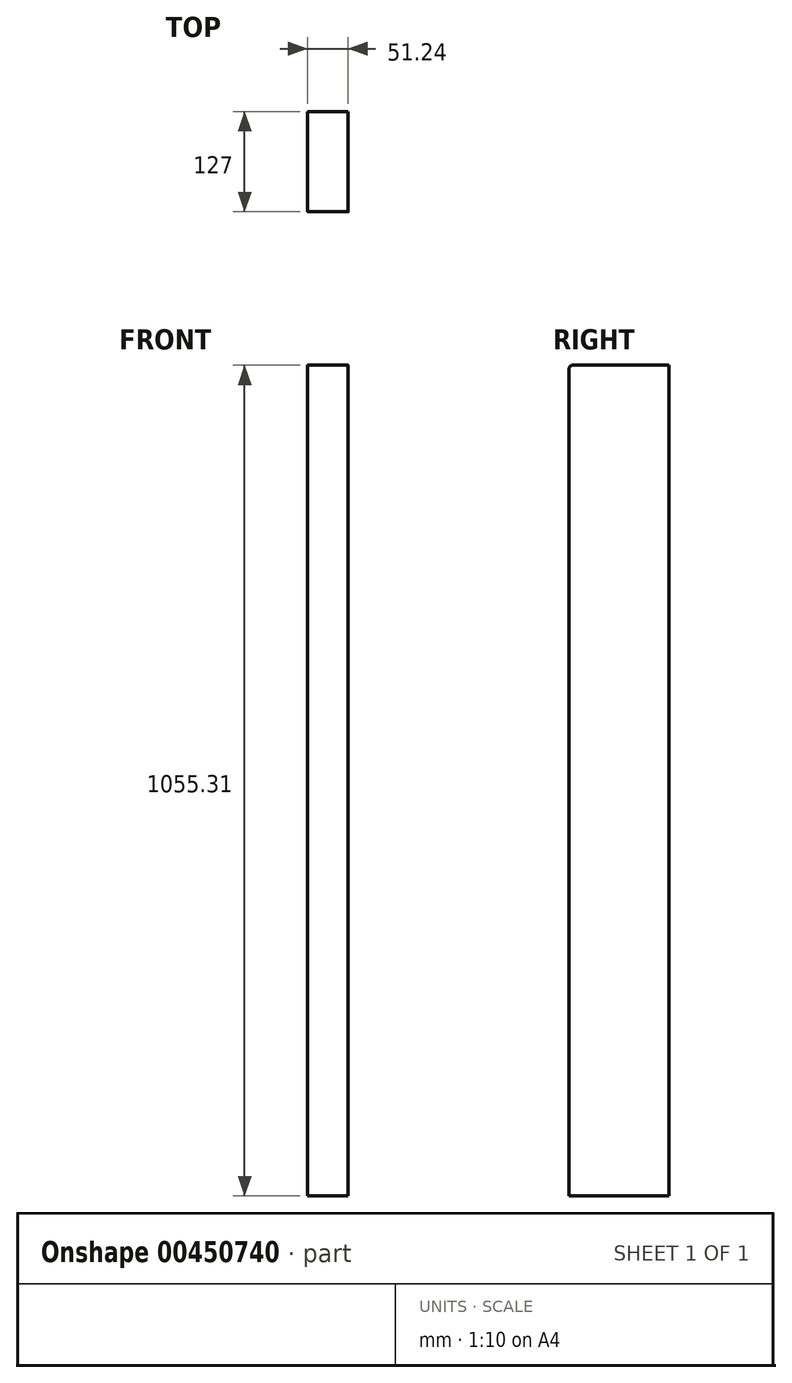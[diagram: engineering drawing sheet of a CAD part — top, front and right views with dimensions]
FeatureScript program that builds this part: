
annotation { "Feature Type Name" : "Feature", "Feature Type Description" : "" }
export const myFeature = defineFeature(function(context is Context, id is Id, definition is map)
    precondition{}
    {
        {
            var Q0;
            Q0=qCreatedBy(makeId("Front.planeOp"),FACE);
            var sketch = newSketch(context, id + "F0", { "sketchPlane" : qUnion([Q0])});
            skLineSegment(sketch, "E0.bottom", {"start": v(0, 0) * mm, "end": v(51.24, 0) * mm});
            skLineSegment(sketch, "E0.top", {"start": v(0, -48.13) * mm, "end": v(51.24, -48.13) * mm});
            skLineSegment(sketch, "E0.left", {"start": v(0, 0) * mm, "end": v(0, -48.13) * mm});
            skLineSegment(sketch, "E0.right", {"start": v(51.24, 0) * mm, "end": v(51.24, -48.13) * mm});
            skSolve(sketch);
        }
        {
            var Q0;
            Q0=makeQuery(id+"F0.imprint","IMPRINT",FACE,{"disambiguationData":[TD([[makeQuery(id+"F0.imprint","IMPRINT",EDGE,{"derivedFrom":sQuery(id+"F0.wireOp",EDGE,"E0.bottom")}),-1.0]])]});
            extrude(context, id + "F1", {"entities" : qUnion([Q0]), "depth" : 127 * mm});
        }
        {
            var Q0;
            Q0=makeQuery(id+"F1.opExtrude","CAP_EDGE",EDGE,{"disambiguationData":[OSD([sQuery(id+"F0.wireOp",EDGE,"E0.bottom")])],"isStart":false});
            fillet(context, id + "F2", {"entities" : qUnion([Q0]), "radius" : 5 * mm, "tangentPropagation" : true, "allowEdgeOverflow" : false});
        }
        {
            var Q0;
            Q0=makeQuery(id+"F1.opExtrude","SWEPT_FACE",FACE,{"disambiguationData":[OSD([sQuery(id+"F0.wireOp",EDGE,"E0.bottom")])]});
            var sketch = newSketch(context, id + "F3", { "sketchPlane" : qUnion([Q0])});
            skCircle(sketch, "E1", {"center": v(26.3, -53.34) * mm, "radius": 18.28 * mm});
            skSolve(sketch);
        }
        {
            var Q0;
            Q0 = qSketchRegion(id + "F3", true);
            var Q1;
            Q1=makeQuery(id+"F1.opExtrude","SWEPT_FACE",FACE,{"disambiguationData":[OSD([sQuery(id+"F0.wireOp",EDGE,"E0.top")])]});
            extrude(context, id + "F4", {"entities" : qUnion([Q0, Q1]), "operationType" : NewBodyOperationType.ADD, "endBound" : BoundingType.THROUGH_ALL, "oppositeDirection" : true, "depth" : 254 * mm});
        }
    });
